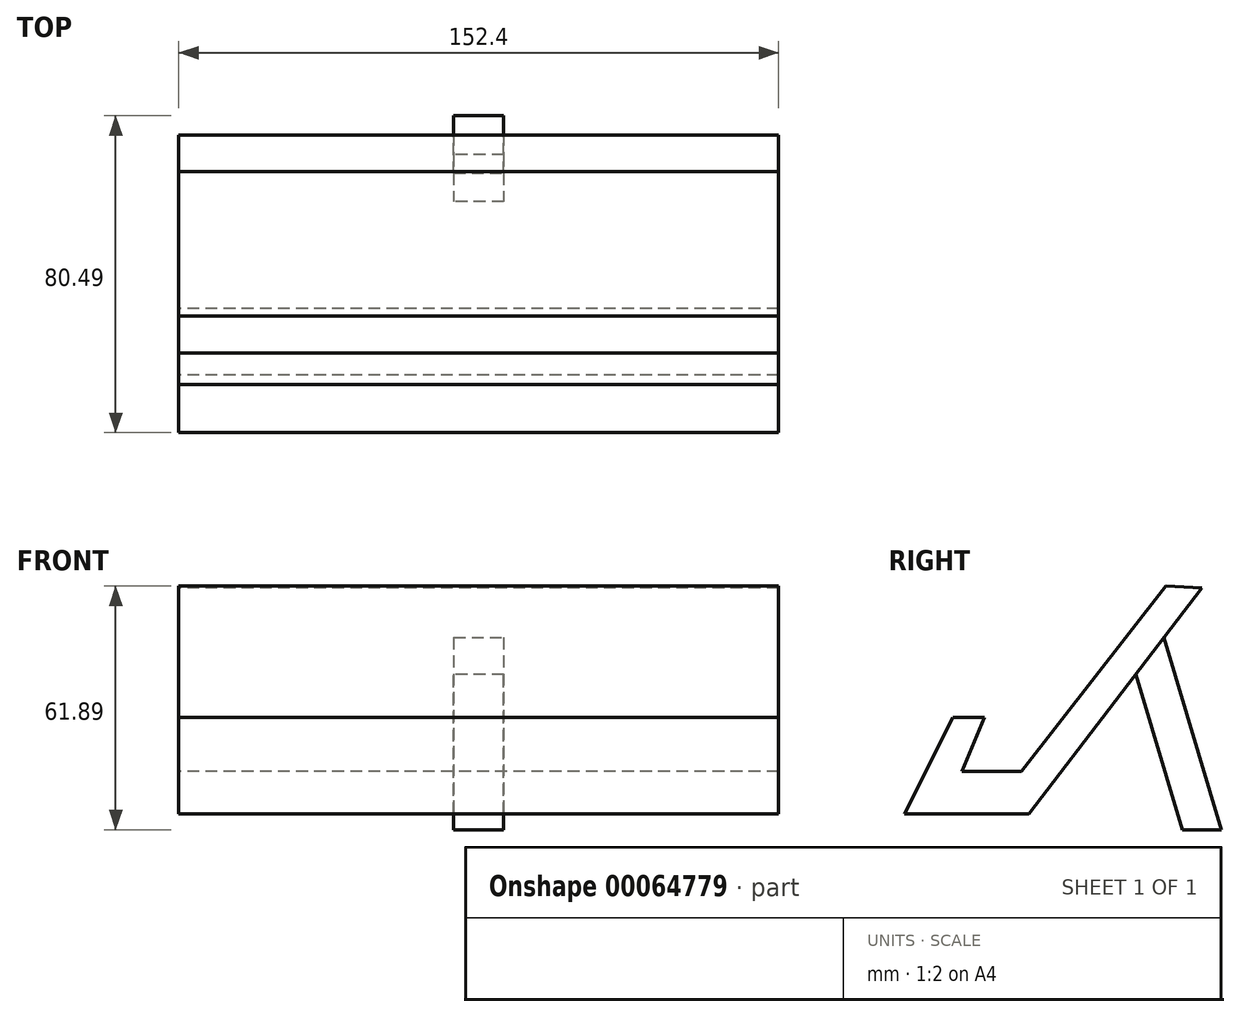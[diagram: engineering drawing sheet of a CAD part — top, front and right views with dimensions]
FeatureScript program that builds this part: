
annotation { "Feature Type Name" : "Feature", "Feature Type Description" : "" }
export const myFeature = defineFeature(function(context is Context, id is Id, definition is map)
    precondition{}
    {
        {
            var Q0;
            Q0=qCreatedBy(makeId("Right.planeOp"),FACE);
            var sketch = newSketch(context, id + "F0", { "sketchPlane" : qUnion([Q0])});
            skLineSegment(sketch, "E0", {"start": v(33.53, 26.36) * mm, "end": v(-10.47, -31.06) * mm});
            skLineSegment(sketch, "E1", {"start": v(-10.47, -31.06) * mm, "end": v(-42, -31.06) * mm});
            skLineSegment(sketch, "E2", {"start": v(-42, -31.06) * mm, "end": v(-29.77, -6.59) * mm});
            skLineSegment(sketch, "E3", {"start": v(-29.77, -6.59) * mm, "end": v(-21.77, -6.59) * mm});
            skLineSegment(sketch, "E4", {"start": v(-21.77, -6.59) * mm, "end": v(-27.42, -20.24) * mm});
            skLineSegment(sketch, "E5", {"start": v(-27.42, -20.24) * mm, "end": v(-12.35, -20.24) * mm});
            skLineSegment(sketch, "E6", {"start": v(-12.35, -20.24) * mm, "end": v(24.36, 26.83) * mm});
            skLineSegment(sketch, "E7", {"start": v(24.36, 26.83) * mm, "end": v(33.53, 26.36) * mm});
            skSolve(sketch);
        }
        {
            var Q0;
            Q0 = qSketchRegion(id + "F0", true);
            extrude(context, id + "F1", {"entities" : qUnion([Q0]), "depth" : 76.2 * mm, "hasSecondDirection" : true, "secondDirectionOppositeDirection" : true, "secondDirectionDepth" : 76.2 * mm});
        }
        {
            var Q0;
            Q0=qCreatedBy(makeId("Right.planeOp"),FACE);
            var sketch = newSketch(context, id + "F2", { "sketchPlane" : qUnion([Q0])});
            skLineSegment(sketch, "E8", {"start": v(22.94, 16.94) * mm, "end": v(38.48, -35.06) * mm});
            skLineSegment(sketch, "E9", {"start": v(38.48, -35.06) * mm, "end": v(28.6, -35.06) * mm});
            skLineSegment(sketch, "E10", {"start": v(28.6, -35.06) * mm, "end": v(15.65, 8) * mm});
            skLineSegment(sketch, "E11", {"start": v(15.65, 8) * mm, "end": v(22.94, 16.94) * mm});
            skSolve(sketch);
        }
        {
            var Q0;
            Q0 = qSketchRegion(id + "F2", true);
            extrude(context, id + "F3", {"entities" : qUnion([Q0]), "operationType" : NewBodyOperationType.ADD, "depth" : 6.35 * mm, "hasSecondDirection" : true, "secondDirectionOppositeDirection" : true, "secondDirectionDepth" : 6.35 * mm});
        }
    });
